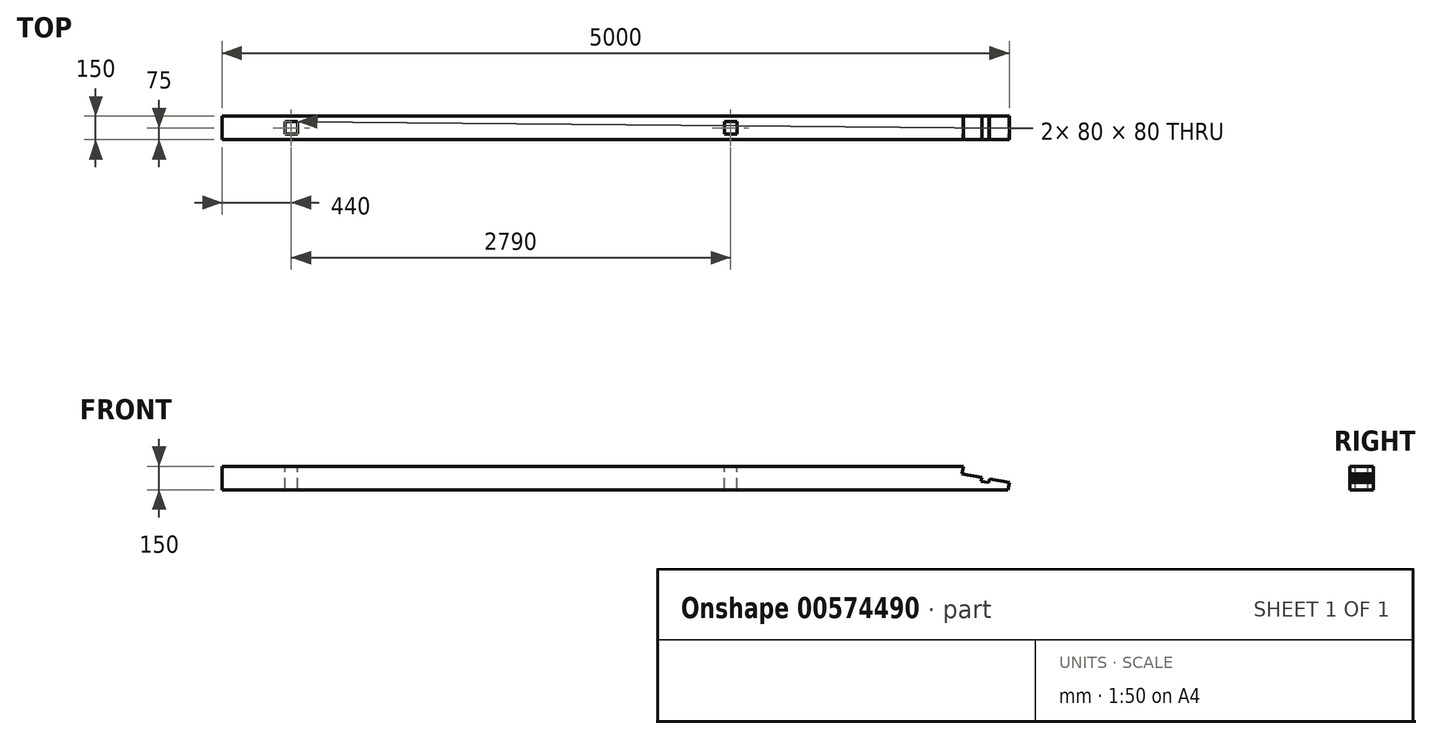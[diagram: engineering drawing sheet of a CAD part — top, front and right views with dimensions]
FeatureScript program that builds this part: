
annotation { "Feature Type Name" : "Feature", "Feature Type Description" : "" }
export const myFeature = defineFeature(function(context is Context, id is Id, definition is map)
    precondition{}
    {
        {
            var Q0;
            Q0=qCreatedBy(makeId("Right.planeOp"),FACE);
            var sketch = newSketch(context, id + "F0", { "sketchPlane" : qUnion([Q0])});
            skLineSegment(sketch, "E0.bottom", {"start": v(75, 75) * mm, "end": v(-75, 75) * mm});
            skLineSegment(sketch, "E0.top", {"start": v(75, -75) * mm, "end": v(-75, -75) * mm});
            skLineSegment(sketch, "E0.left", {"start": v(75, 75) * mm, "end": v(75, -75) * mm});
            skLineSegment(sketch, "E0.right", {"start": v(-75, 75) * mm, "end": v(-75, -75) * mm});
            skPoint(sketch, "E0.middle", {"position": v(0, 0) * mm});
            skSolve(sketch);
        }
        {
            var Q0;
            Q0=makeQuery(id+"F0.imprint","IMPRINT",FACE,{"disambiguationData":[TD([[makeQuery(id+"F0.imprint","IMPRINT",EDGE,{"derivedFrom":sQuery(id+"F0.wireOp",EDGE,"E0.bottom")}),1.0]])]});
            extrude(context, id + "F1", {"entities" : qUnion([Q0]), "depth" : 5000 * mm, "offsetDistance" : 25 * mm});
        }
        {
            var Q0;
            Q0=makeQuery(id+"F1.opExtrude","SWEPT_FACE",FACE,{"disambiguationData":[OSD([sQuery(id+"F0.wireOp",EDGE,"E0.right")])]});
            var sketch = newSketch(context, id + "F2", { "sketchPlane" : qUnion([Q0])});
            skLineSegment(sketch, "E1", {"start": v(4708.56, 75) * mm, "end": v(4700, 26.45) * mm});
            skLineSegment(sketch, "E2", {"start": v(4700, 26.45) * mm, "end": v(5000, -26.45) * mm});
            skLineSegment(sketch, "E3", {"start": v(5000, -26.45) * mm, "end": v(4991.44, -75) * mm});
            skLineSegment(sketch, "E4", {"start": v(4708.56, 75) * mm, "end": v(5050, 75) * mm});
            skLineSegment(sketch, "E5", {"start": v(5050, 75) * mm, "end": v(5050, -75) * mm});
            skLineSegment(sketch, "E6", {"start": v(5050, -75) * mm, "end": v(4991.44, -75) * mm});
            skLineSegment(sketch, "E7", {"start": v(4850, 0) * mm, "end": v(4845.66, -24.62) * mm, "construction": true});
            skLineSegment(sketch, "E8", {"start": v(4825.38, 4.34) * mm, "end": v(4821.04, -20.28) * mm});
            skLineSegment(sketch, "E9", {"start": v(4821.04, -20.28) * mm, "end": v(4870.28, -28.96) * mm});
            skLineSegment(sketch, "E10", {"start": v(4870.28, -28.96) * mm, "end": v(4874.62, -4.34) * mm});
            skSolve(sketch);
        }
        {
            var Q0;
            {var subQ0=sQuery(id+"F2.wireOp",EDGE,"E3");Q0=makeQuery(id+"F2.imprint","IMPRINT",FACE,{"disambiguationData":[TD([[makeQuery(id+"F2.imprint","IMPRINT",EDGE,{"derivedFrom":subQ0}),1.0]])]});}
            var Q1;
            {var subQ6=sQuery(id+"F2.wireOp",EDGE,"E5");Q1=makeQuery(id+"F2.imprint","IMPRINT",FACE,{"disambiguationData":[TD([[makeQuery(id+"F2.imprint","IMPRINT",EDGE,{"derivedFrom":subQ6}),-1.0]])]});}
            var Q2;
            {var subQ0=sQuery(id+"F2.wireOp",EDGE,"E8");Q2=makeQuery(id+"F2.imprint","IMPRINT",FACE,{"disambiguationData":[TD([[makeQuery(id+"F2.imprint","IMPRINT",EDGE,{"derivedFrom":subQ0}),1.0]])]});}
            var Q3;
            {var subQ6=sQuery(id+"F2.wireOp",EDGE,"E1");Q3=makeQuery(id+"F2.imprint","IMPRINT",FACE,{"disambiguationData":[TD([[makeQuery(id+"F2.imprint","IMPRINT",EDGE,{"derivedFrom":subQ6}),1.0]])]});}
            extrude(context, id + "F3", {"entities" : qUnion([Q0, Q1, Q2, Q3]), "operationType" : NewBodyOperationType.REMOVE, "endBound" : BoundingType.THROUGH_ALL, "oppositeDirection" : true, "depth" : 25 * mm, "offsetDistance" : 25 * mm});
        }
        {
            var Q0;
            Q0=makeQuery(id+"F1.opExtrude","SWEPT_FACE",FACE,{"disambiguationData":[OSD([sQuery(id+"F0.wireOp",EDGE,"E0.bottom")])]});
            var sketch = newSketch(context, id + "F4", { "sketchPlane" : qUnion([Q0])});
            skLineSegment(sketch, "E11.bottom", {"start": v(3190, 40) * mm, "end": v(3270, 40) * mm});
            skLineSegment(sketch, "E11.top", {"start": v(3190, -40) * mm, "end": v(3270, -40) * mm});
            skLineSegment(sketch, "E11.left", {"start": v(3190, 40) * mm, "end": v(3190, -40) * mm});
            skLineSegment(sketch, "E11.right", {"start": v(3270, 40) * mm, "end": v(3270, -40) * mm});
            skPoint(sketch, "E11.middle", {"position": v(3230, 0) * mm});
            skLineSegment(sketch, "E12.bottom", {"start": v(480, 40) * mm, "end": v(400, 40) * mm});
            skLineSegment(sketch, "E12.top", {"start": v(480, -40) * mm, "end": v(400, -40) * mm});
            skLineSegment(sketch, "E12.left", {"start": v(480, 40) * mm, "end": v(480, -40) * mm});
            skLineSegment(sketch, "E12.right", {"start": v(400, 40) * mm, "end": v(400, -40) * mm});
            skPoint(sketch, "E12.middle", {"position": v(440, 0) * mm});
            skSolve(sketch);
        }
        {
            var Q0;
            Q0=makeQuery(id+"F4.imprint","IMPRINT",FACE,{"disambiguationData":[TD([[makeQuery(id+"F4.imprint","IMPRINT",EDGE,{"derivedFrom":sQuery(id+"F4.wireOp",EDGE,"E12.bottom")}),1.0]])]});
            var Q1;
            Q1=makeQuery(id+"F4.imprint","IMPRINT",FACE,{"disambiguationData":[TD([[makeQuery(id+"F4.imprint","IMPRINT",EDGE,{"derivedFrom":sQuery(id+"F4.wireOp",EDGE,"E11.bottom")}),-1.0]])]});
            extrude(context, id + "F5", {"entities" : qUnion([Q0, Q1]), "operationType" : NewBodyOperationType.REMOVE, "endBound" : BoundingType.UP_TO_NEXT, "oppositeDirection" : true, "depth" : 25 * mm, "offsetDistance" : 25 * mm});
        }
    });
